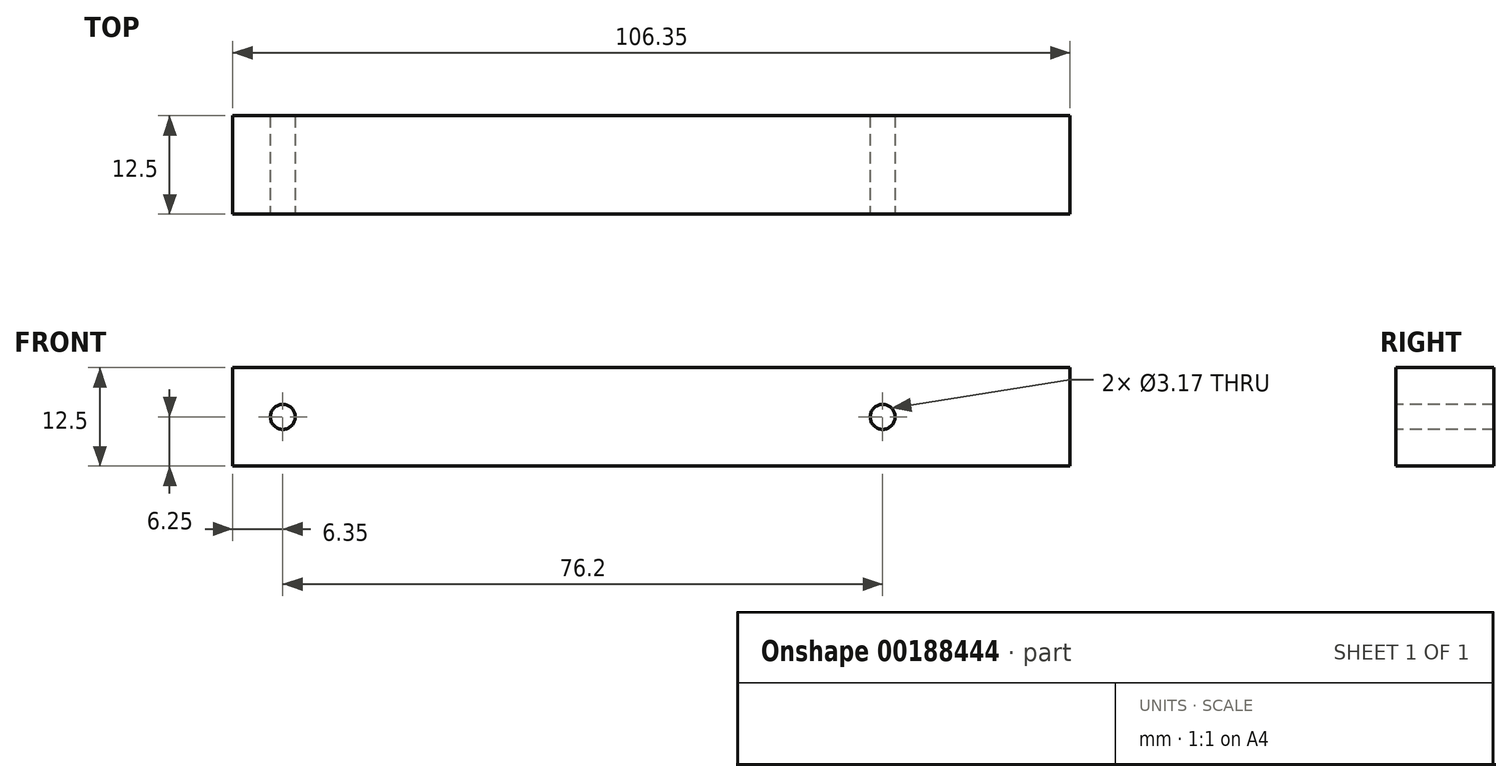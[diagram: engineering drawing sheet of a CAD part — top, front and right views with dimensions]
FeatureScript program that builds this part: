
annotation { "Feature Type Name" : "Feature", "Feature Type Description" : "" }
export const myFeature = defineFeature(function(context is Context, id is Id, definition is map)
    precondition{}
    {
        {
            var Q0;
            Q0=qCreatedBy(makeId("Right.planeOp"),FACE);
            var sketch = newSketch(context, id + "F0", { "sketchPlane" : qUnion([Q0])});
            skLineSegment(sketch, "E0.bottom", {"start": v(-6.25, 6.25) * mm, "end": v(6.25, 6.25) * mm});
            skLineSegment(sketch, "E0.top", {"start": v(-6.25, -6.25) * mm, "end": v(6.25, -6.25) * mm});
            skLineSegment(sketch, "E0.left", {"start": v(-6.25, 6.25) * mm, "end": v(-6.25, -6.25) * mm});
            skLineSegment(sketch, "E0.right", {"start": v(6.25, 6.25) * mm, "end": v(6.25, -6.25) * mm});
            skPoint(sketch, "E0.middle", {"position": v(0, 0) * mm});
            skSolve(sketch);
        }
        {
            var Q0;
            Q0 = qSketchRegion(id + "F0", true);
            extrude(context, id + "F1", {"entities" : qUnion([Q0]), "depth" : 106.35 * mm, "offsetDistance" : 25 * mm});
        }
        {
            var Q0;
            Q0=makeQuery(id+"F1.opExtrude","SWEPT_FACE",FACE,{"disambiguationData":[OSD([sQuery(id+"F0.wireOp",EDGE,"E0.left")])]});
            var sketch = newSketch(context, id + "F2", { "sketchPlane" : qUnion([Q0])});
            skPoint(sketch, "E1", {"position": v(6.35, 0) * mm});
            skPoint(sketch, "E2", {"position": v(82.55, 0) * mm});
            skLineSegment(sketch, "E3", {"start": v(0, 0) * mm, "end": v(106.35, 0) * mm, "construction": true});
            skSolve(sketch);
        }
        {
            var Q0;
            Q0=sQuery(id+"F2.wireOp",VERTEX,"E1");
            var Q1;
            Q1=sQuery(id+"F2.wireOp",VERTEX,"E2");
            var Q2;
            Q2=makeQuery(id+"F1.opExtrude","SWEPT_BODY",BODY,{"disambiguationData":[OSD([sQuery(id+"F0.wireOp",EDGE,"E0.bottom"),sQuery(id+"F0.wireOp",EDGE,"E0.top"),sQuery(id+"F0.wireOp",EDGE,"E0.left"),sQuery(id+"F0.wireOp",EDGE,"E0.right")])]});
            hole(context, id + "F3", {"style" : HoleStyle.SIMPLE, "endStyle" : HoleEndStyle.THROUGH, "holeDiameter" : 3.17 * mm, "majorDiameter" : 5 * mm, "isTappedThrough" : true, "tappedDepth" : 12 * mm, "tapClearance" : 3, "startFromSketch" : true, "locations" : qUnion([Q0, Q1]), "scope" : qUnion([Q2])});
        }
    });
